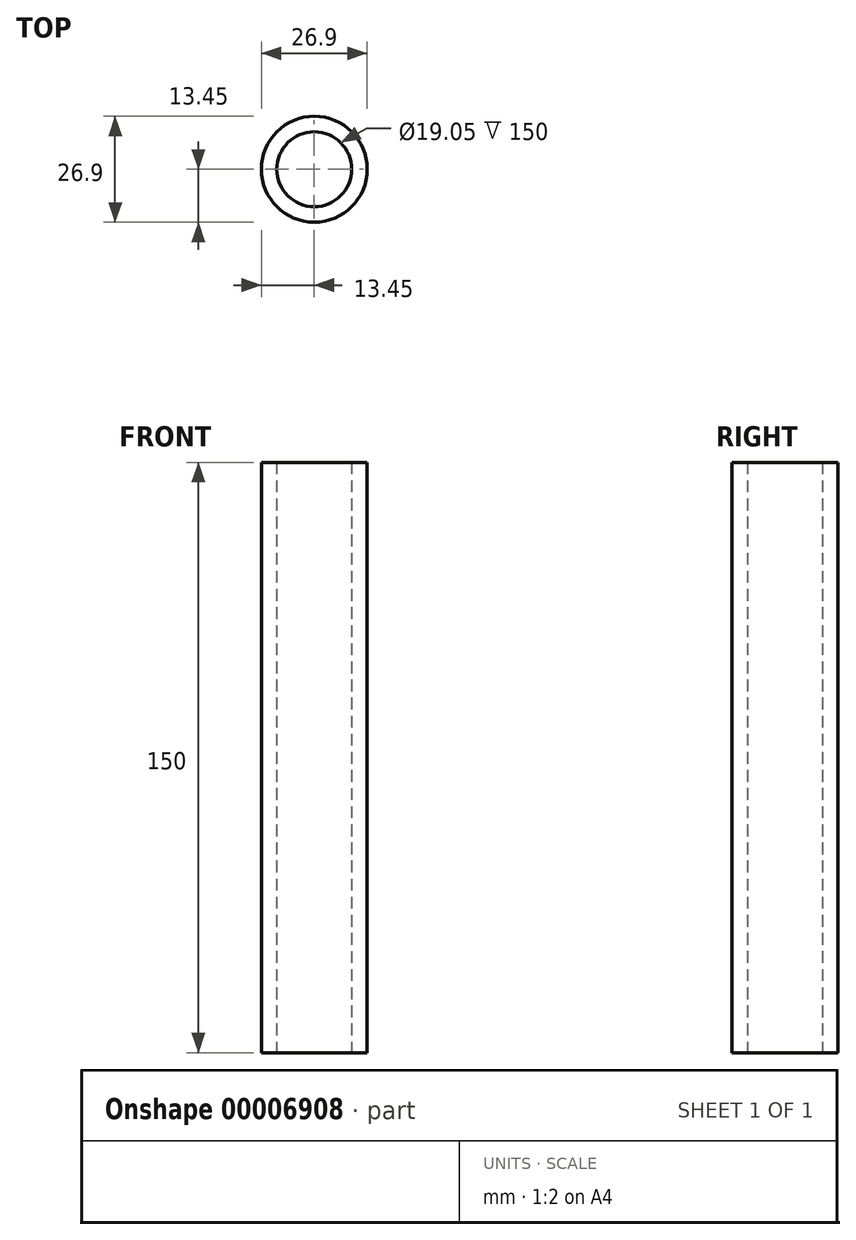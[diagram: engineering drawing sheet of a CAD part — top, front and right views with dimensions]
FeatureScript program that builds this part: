
annotation { "Feature Type Name" : "Feature", "Feature Type Description" : "" }
export const myFeature = defineFeature(function(context is Context, id is Id, definition is map)
    precondition{}
    {
        {
            var Q0;
            Q0=qCreatedBy(makeId("Top.planeOp"),FACE);
            var sketch = newSketch(context, id + "F0", { "sketchPlane" : qUnion([Q0])});
            skCircle(sketch, "E0", {"center": v(0, 0) * mm, "radius": 13.45 * mm});
            skCircle(sketch, "E1", {"center": v(0, 0) * mm, "radius": 9.53 * mm});
            skSolve(sketch);
        }
        {
            var Q0;
            Q0=makeQuery(id+"F0.imprint","IMPRINT",FACE,{"disambiguationData":[TD([[makeQuery(id+"F0.imprint","IMPRINT",EDGE,{"derivedFrom":sQuery(id+"F0.wireOp",EDGE,"E0")}),1.0]])]});
            extrude(context, id + "F1", {"entities" : qUnion([Q0]), "depth" : (150) * mm});
        }
    });
